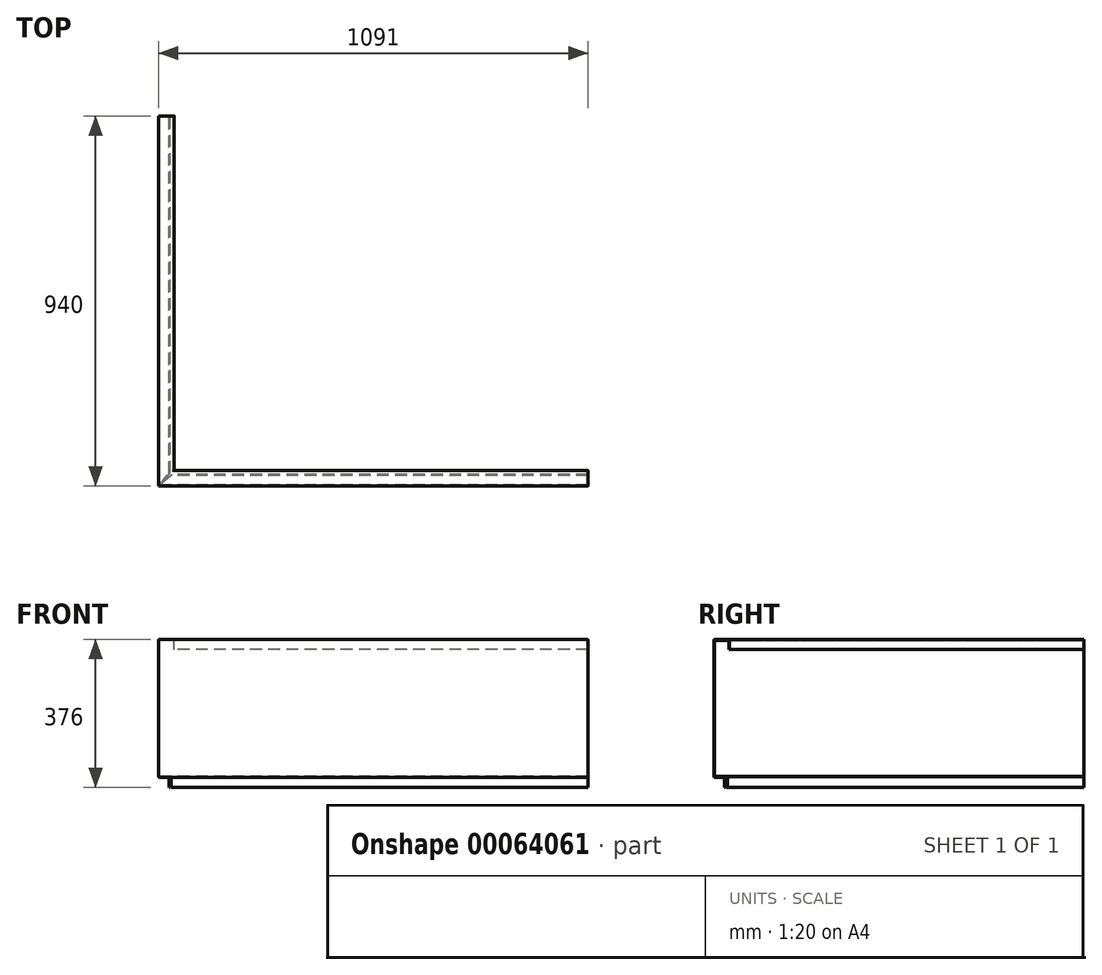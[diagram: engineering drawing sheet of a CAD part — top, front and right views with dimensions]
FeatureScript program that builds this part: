
annotation { "Feature Type Name" : "Feature", "Feature Type Description" : "" }
export const myFeature = defineFeature(function(context is Context, id is Id, definition is map)
    precondition{}
    {
        {
            var Q0;
            Q0=qCreatedBy(makeId("Right.planeOp"),FACE);
            var sketch = newSketch(context, id + "F0", { "sketchPlane" : qUnion([Q0])});
            skLineSegment(sketch, "E0.0", {"start": v(0, -350) * mm, "end": v(27, -350) * mm});
            skLineSegment(sketch, "E0.1", {"start": v(0, 0) * mm, "end": v(0, -350) * mm});
            skLineSegment(sketch, "E1", {"start": v(2, -348) * mm, "end": v(29, -348) * mm});
            skLineSegment(sketch, "E2", {"start": v(2, -2) * mm, "end": v(2, -348) * mm});
            skLineSegment(sketch, "E3", {"start": v(38, -2) * mm, "end": v(2, -2) * mm});
            skLineSegment(sketch, "E4", {"start": v(38, -25) * mm, "end": v(38, -2) * mm});
            skLineSegment(sketch, "E5", {"start": v(27, -350) * mm, "end": v(27, -376) * mm});
            skLineSegment(sketch, "E6", {"start": v(29, -348) * mm, "end": v(29, -376) * mm});
            skLineSegment(sketch, "E0.2", {"start": v(40, 0) * mm, "end": v(0, 0) * mm});
            skLineSegment(sketch, "E0.3", {"start": v(40, -25) * mm, "end": v(40, 0) * mm});
            skLineSegment(sketch, "E7", {"start": v(40, -25) * mm, "end": v(38, -25) * mm});
            skLineSegment(sketch, "E8", {"start": v(29, -376) * mm, "end": v(27, -376) * mm});
            skSolve(sketch);
        }
        {
            var Q0;
            Q0=qCreatedBy(makeId("Top.planeOp"),FACE);
            var sketch = newSketch(context, id + "F1", { "sketchPlane" : qUnion([Q0])});
            skLineSegment(sketch, "E9", {"start": v(0, 0) * mm, "end": v(-1091, 0) * mm});
            skLineSegment(sketch, "E10", {"start": v(-1091, 0) * mm, "end": v(-1091, 940) * mm});
            skSolve(sketch);
        }
        {
            var Q0;
            Q0=qSketchRegion(id+"F0",true);
            var Q1;
            Q1=qConstructionFilter(qBodyType(qCreatedBy(id+"F1",EDGE),BodyType.WIRE),ConstructionObject.NO);
            sweep(context, id + "F2", {"profiles" : qUnion([Q0]), "path" : qUnion([Q1])});
        }
        {
            var Q0;
            Q0=makeQuery(id+"F2.opSweep","SWEPT_FACE",FACE,{"disambiguationData":[OSD([sQuery(id+"F0.wireOp",EDGE,"E1"),sQuery(id+"F1.wireOp",EDGE,"E9")])]});
            var sketch = newSketch(context, id + "F3", { "sketchPlane" : qUnion([Q0])});
            skLineSegment(sketch, "E11", {"start": v(-1089, 2) * mm, "end": v(-1062, 34.18) * mm});
            skLineSegment(sketch, "E12", {"start": v(-1062, 34.18) * mm, "end": v(-1056.82, 29) * mm});
            skLineSegment(sketch, "E13", {"start": v(-1056.82, 29) * mm, "end": v(-1089, 2) * mm});
            skSolve(sketch);
        }
        {
            var Q0;
            Q0=qSketchRegion(id+"F3",true);
            extrude(context, id + "F4", {"entities" : qUnion([Q0]), "operationType" : NewBodyOperationType.REMOVE, "oppositeDirection" : true, "depth" : 30 * mm});
        }
        {
            var Q0;
            Q0=makeQuery(id+"F2.opSweep","SWEPT_EDGE",EDGE,{"disambiguationData":[OSD([sQuery(id+"F0.wireOp",EDGE,"E1"),sQuery(id+"F0.wireOp",EDGE,"E6"),sQuery(id+"F1.wireOp",EDGE,"E10")])]});
            var Q1;
            Q1=makeQuery(id+"F2.opSweep","SWEPT_EDGE",EDGE,{"disambiguationData":[OSD([sQuery(id+"F0.wireOp",EDGE,"E1"),sQuery(id+"F0.wireOp",EDGE,"E2"),sQuery(id+"F1.wireOp",EDGE,"E10")])]});
            var Q2;
            Q2=makeQuery(id+"F2.opSweep","SWEPT_EDGE",EDGE,{"disambiguationData":[OSD([sQuery(id+"F0.wireOp",EDGE,"E0.2"),sQuery(id+"F0.wireOp",EDGE,"E0.3"),sQuery(id+"F1.wireOp",EDGE,"E10")])]});
            var Q3;
            Q3=makeQuery(id+"F2.opSweep","SWEPT_EDGE",EDGE,{"disambiguationData":[OSD([sQuery(id+"F0.wireOp",EDGE,"E0.0"),sQuery(id+"F0.wireOp",EDGE,"E5"),sQuery(id+"F1.wireOp",EDGE,"E10")])]});
            var Q4;
            Q4=makeQuery(id+"F2.opSweep","SWEPT_EDGE",EDGE,{"disambiguationData":[OSD([sQuery(id+"F0.wireOp",EDGE,"E0.0"),sQuery(id+"F0.wireOp",EDGE,"E0.1"),sQuery(id+"F1.wireOp",EDGE,"E10")])]});
            var Q5;
            Q5=makeQuery(id+"F2.opSweep","SWEPT_EDGE",EDGE,{"disambiguationData":[OSD([sQuery(id+"F0.wireOp",EDGE,"E0.1"),sQuery(id+"F0.wireOp",EDGE,"E0.2"),sQuery(id+"F1.wireOp",EDGE,"E10")])]});
            var Q6;
            Q6=makeQuery(id+"F2.opSweep","SWEPT_EDGE",EDGE,{"disambiguationData":[OSD([sQuery(id+"F0.wireOp",EDGE,"E3"),sQuery(id+"F0.wireOp",EDGE,"E4"),sQuery(id+"F1.wireOp",EDGE,"E10")])]});
            var Q7;
            Q7=makeQuery(id+"F2.opSweep","SWEPT_EDGE",EDGE,{"disambiguationData":[OSD([sQuery(id+"F0.wireOp",EDGE,"E2"),sQuery(id+"F0.wireOp",EDGE,"E3"),sQuery(id+"F1.wireOp",EDGE,"E10")])]});
            var Q8;
            Q8=makeQuery(id+"F2.opSweep","SWEPT_EDGE",EDGE,{"disambiguationData":[OSD([sQuery(id+"F0.wireOp",EDGE,"E0.0"),sQuery(id+"F0.wireOp",EDGE,"E5"),sQuery(id+"F1.wireOp",EDGE,"E9")])]});
            var Q9;
            Q9=makeQuery(id+"F2.opSweep","SWEPT_EDGE",EDGE,{"disambiguationData":[OSD([sQuery(id+"F0.wireOp",EDGE,"E1"),sQuery(id+"F0.wireOp",EDGE,"E6"),sQuery(id+"F1.wireOp",EDGE,"E9")])]});
            var Q10;
            Q10=makeQuery(id+"F2.opSweep","SWEPT_EDGE",EDGE,{"disambiguationData":[OSD([sQuery(id+"F0.wireOp",EDGE,"E0.0"),sQuery(id+"F0.wireOp",EDGE,"E0.1"),sQuery(id+"F1.wireOp",EDGE,"E9")])]});
            var Q11;
            Q11=makeQuery(id+"F2.opSweep","SWEPT_EDGE",EDGE,{"disambiguationData":[OSD([sQuery(id+"F0.wireOp",EDGE,"E1"),sQuery(id+"F0.wireOp",EDGE,"E2"),sQuery(id+"F1.wireOp",EDGE,"E9")])]});
            var Q12;
            Q12=makeQuery(id+"F2.opSweep","SWEPT_EDGE",EDGE,{"disambiguationData":[OSD([sQuery(id+"F0.wireOp",EDGE,"E0.2"),sQuery(id+"F0.wireOp",EDGE,"E0.3"),sQuery(id+"F1.wireOp",EDGE,"E9")])]});
            var Q13;
            Q13=makeQuery(id+"F2.opSweep","SWEPT_EDGE",EDGE,{"disambiguationData":[OSD([sQuery(id+"F0.wireOp",EDGE,"E0.1"),sQuery(id+"F0.wireOp",EDGE,"E0.2"),sQuery(id+"F1.wireOp",EDGE,"E9")])]});
            var Q14;
            Q14=makeQuery(id+"F2.opSweep","SWEPT_EDGE",EDGE,{"disambiguationData":[OSD([sQuery(id+"F0.wireOp",EDGE,"E2"),sQuery(id+"F0.wireOp",EDGE,"E3"),sQuery(id+"F1.wireOp",EDGE,"E9")])]});
            var Q15;
            Q15=makeQuery(id+"F2.opSweep","SWEPT_EDGE",EDGE,{"disambiguationData":[OSD([sQuery(id+"F0.wireOp",EDGE,"E3"),sQuery(id+"F0.wireOp",EDGE,"E4"),sQuery(id+"F1.wireOp",EDGE,"E9")])]});
            fillet(context, id + "F5", {"entities" : qUnion([Q0, Q1, Q2, Q3, Q4, Q5, Q6, Q7, Q8, Q9, Q10, Q11, Q12, Q13, Q14, Q15]), "radius" : 2 * mm, "tangentPropagation" : true, "allowEdgeOverflow" : false});
        }
    });
